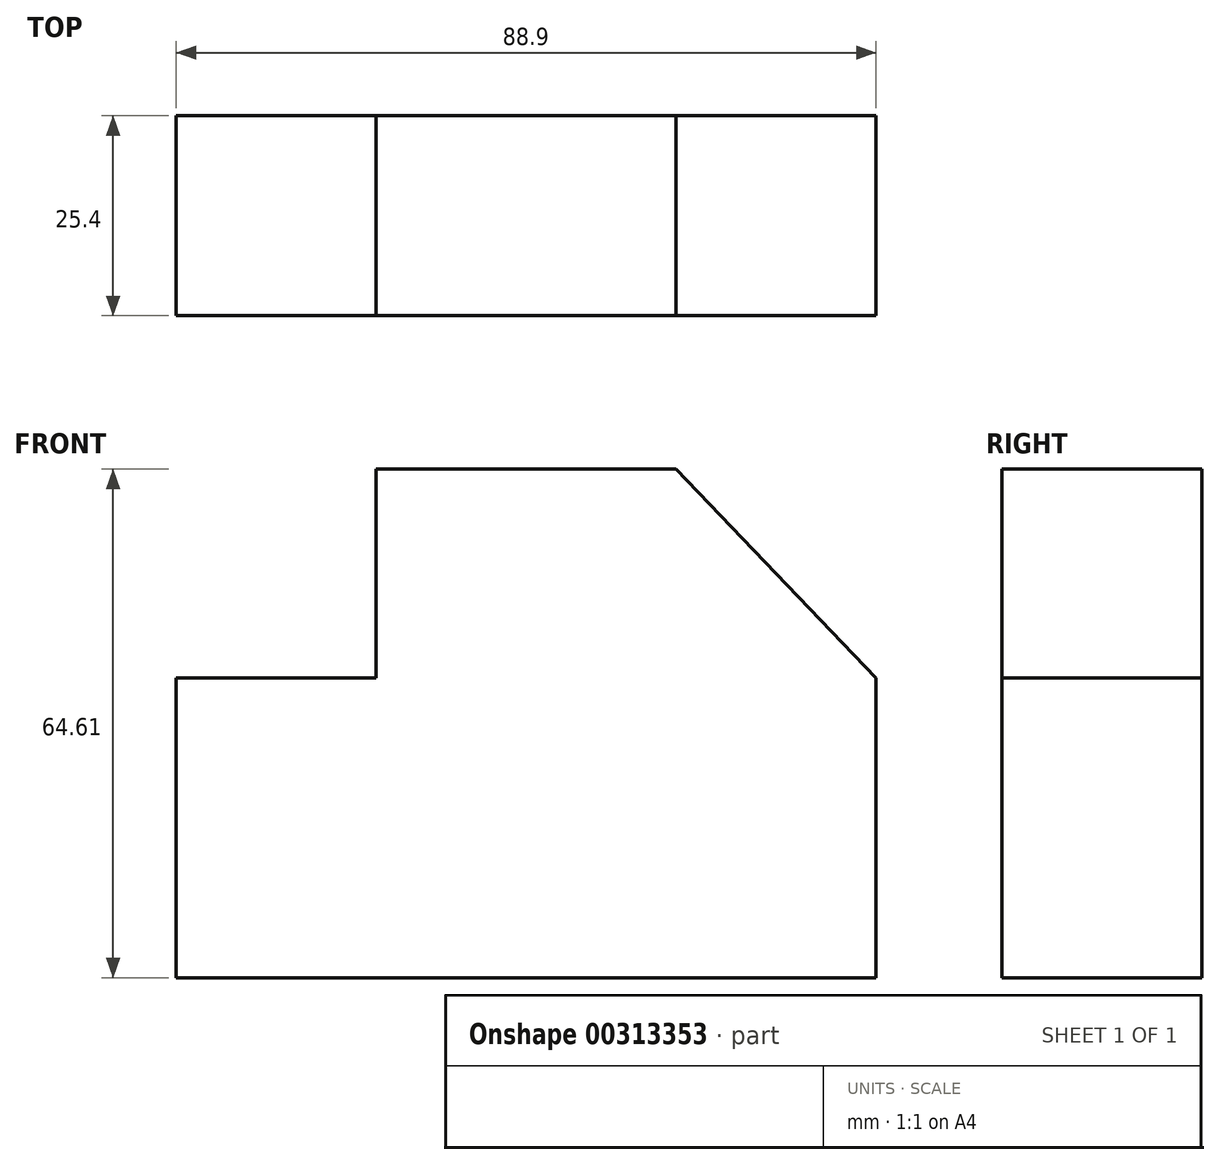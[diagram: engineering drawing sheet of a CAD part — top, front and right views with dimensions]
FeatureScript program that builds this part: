
annotation { "Feature Type Name" : "Feature", "Feature Type Description" : "" }
export const myFeature = defineFeature(function(context is Context, id is Id, definition is map)
    precondition{}
    {
        {
            var Q0;
            Q0=qCreatedBy(makeId("Front.planeOp"),FACE);
            var sketch = newSketch(context, id + "F0", { "sketchPlane" : qUnion([Q0])});
            skLineSegment(sketch, "E0", {"start": v(-46.27, -47.5) * mm, "end": v(42.63, -47.5) * mm});
            skLineSegment(sketch, "E1", {"start": v(-46.27, -47.5) * mm, "end": v(-46.27, -9.4) * mm});
            skLineSegment(sketch, "E2", {"start": v(-46.27, -9.4) * mm, "end": v(-20.87, -9.4) * mm});
            skLineSegment(sketch, "E3", {"start": v(-20.87, -9.4) * mm, "end": v(-20.87, 17.11) * mm});
            skLineSegment(sketch, "E4", {"start": v(-20.87, 17.11) * mm, "end": v(17.23, 17.11) * mm});
            skLineSegment(sketch, "E5", {"start": v(17.23, 17.11) * mm, "end": v(42.63, -9.4) * mm});
            skLineSegment(sketch, "E6", {"start": v(42.63, -9.4) * mm, "end": v(42.63, -47.5) * mm});
            skSolve(sketch);
        }
        {
            var Q0;
            Q0=makeQuery(id+"F0.imprint","IMPRINT",FACE,{"disambiguationData":[TD([[makeQuery(id+"F0.imprint","IMPRINT",EDGE,{"derivedFrom":sQuery(id+"F0.wireOp",EDGE,"E0")}),1.0]])]});
            extrude(context, id + "F1", {"entities" : qUnion([Q0]), "depth" : 25.4 * mm});
        }
    });
